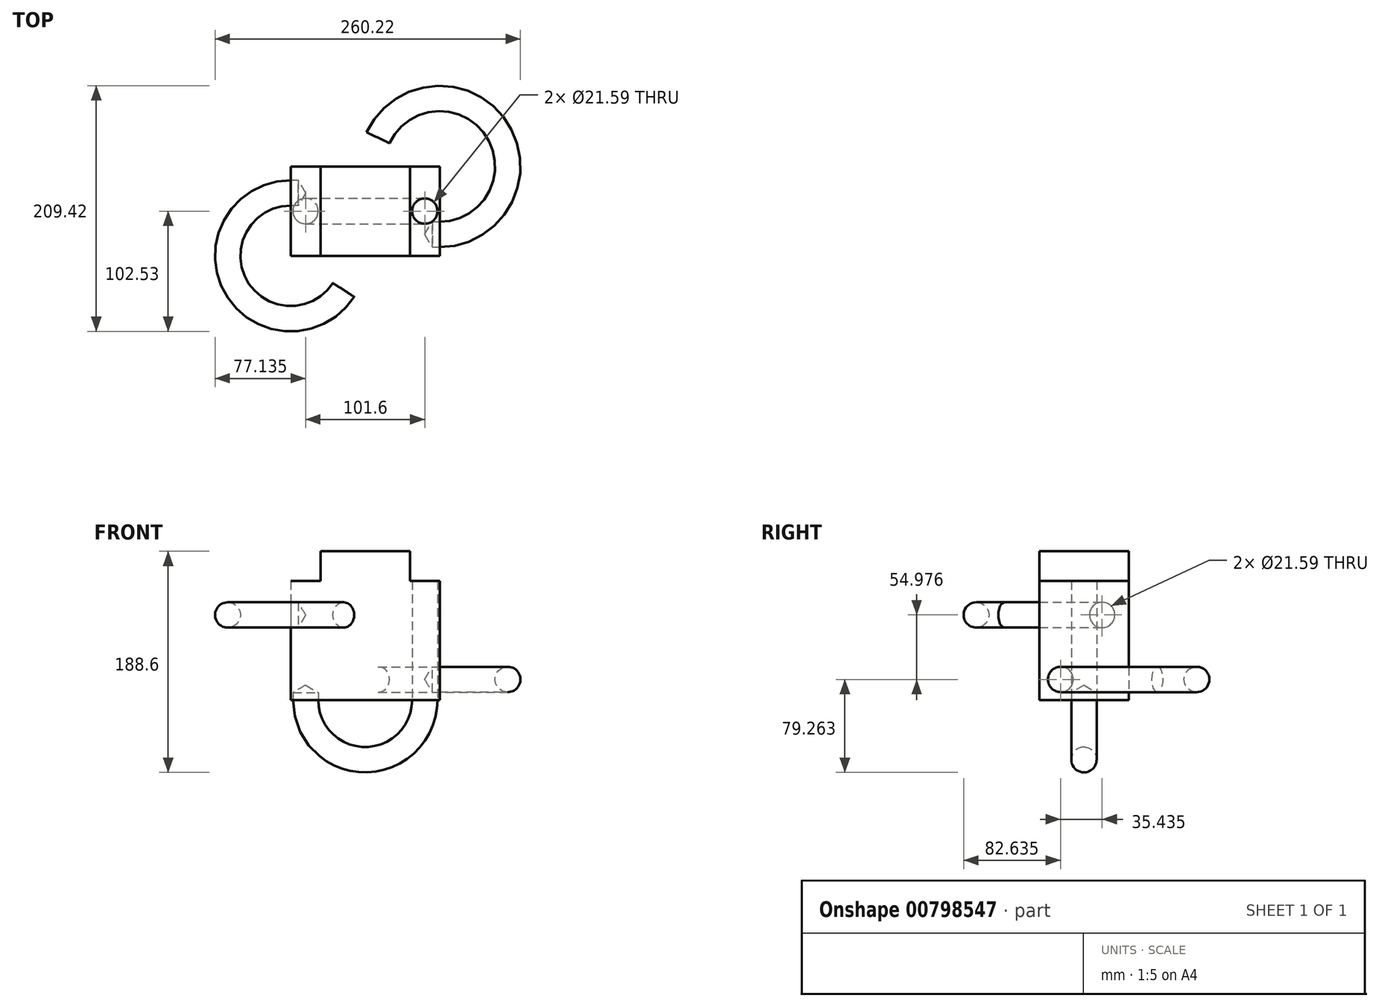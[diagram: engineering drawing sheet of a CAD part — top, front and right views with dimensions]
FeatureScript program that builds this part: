
annotation { "Feature Type Name" : "Feature", "Feature Type Description" : "" }
export const myFeature = defineFeature(function(context is Context, id is Id, definition is map)
    precondition{}
    {
        {
            var Q0;
            Q0=qCreatedBy(makeId("Top.planeOp"),FACE);
            var sketch = newSketch(context, id + "F0", { "sketchPlane" : qUnion([Q0])});
            skLineSegment(sketch, "E0.bottom", {"start": v(-20.13, 76.2) * mm, "end": v(106.87, 76.2) * mm});
            skLineSegment(sketch, "E0.top", {"start": v(-20.13, 0) * mm, "end": v(106.87, 0) * mm});
            skLineSegment(sketch, "E0.left", {"start": v(-20.13, 76.2) * mm, "end": v(-20.13, 0) * mm});
            skLineSegment(sketch, "E0.right", {"start": v(106.87, 76.2) * mm, "end": v(106.87, 0) * mm});
            skLineSegment(sketch, "E1.bottom", {"start": v(5.27, 76.2) * mm, "end": v(81.47, 76.2) * mm});
            skLineSegment(sketch, "E1.top", {"start": v(5.27, 0) * mm, "end": v(81.47, 0) * mm});
            skLineSegment(sketch, "E1.left", {"start": v(5.27, 76.2) * mm, "end": v(5.27, 0) * mm});
            skLineSegment(sketch, "E1.right", {"start": v(81.47, 76.2) * mm, "end": v(81.47, 0) * mm});
            skCircle(sketch, "E2", {"center": v(-7.43, 38.1) * mm, "radius": 10.8 * mm});
            skPoint(sketch, "E2.centerSnap0", {"position": v(-20.13, 38.1) * mm});
            skLineSegment(sketch, "E3", {"start": v(43.37, 0) * mm, "end": v(43.37, 76.2) * mm, "construction": true});
            skCircle(sketch, "E4.MirrorC", {"center": v(94.17, 38.1) * mm, "radius": 10.8 * mm});
            skSolve(sketch);
        }
        {
            var Q0;
            {var subQ0=sQuery(id+"F0.wireOp",EDGE,"E1.left");var subQ8=makeQuery(id+"F0.imprint","IMPRINT",EDGE,{"derivedFrom":subQ0});var subQ10=sQuery(id+"F0.wireOp",EDGE,"E0.left");var subQ11=sQuery(id+"F0.wireOp",EDGE,"E0.right");Q0=qUnion([makeQuery(id+"F0.imprint","IMPRINT",FACE,{"disambiguationData":[TD([[makeQuery(id+"F0.imprint","IMPRINT",EDGE,{"derivedFrom":subQ11}),-1.0]])]}),makeQuery(id+"F0.imprint","IMPRINT",FACE,{"disambiguationData":[TD([[makeQuery(id+"F0.imprint","IMPRINT",EDGE,{"derivedFrom":subQ10}),1.0]])]}),makeQuery(id+"F0.imprint","IMPRINT",FACE,{"disambiguationData":[TD([[subQ8,1.0]])]})]);}
            var Q1;
            Q1=makeQuery(id+"F0.imprint","IMPRINT",FACE,{"disambiguationData":[TD([[makeQuery(id+"F0.imprint","IMPRINT",EDGE,{"derivedFrom":sQuery(id+"F0.wireOp",EDGE,"E2")}),1.0]])]});
            var Q2;
            Q2=makeQuery(id+"F0.imprint","IMPRINT",FACE,{"disambiguationData":[TD([[makeQuery(id+"F0.imprint","IMPRINT",EDGE,{"derivedFrom":sQuery(id+"F0.wireOp",EDGE,"E4.MirrorC")}),-1.0]])]});
            extrude(context, id + "F1", {"entities" : qUnion([Q0, Q1, Q2]), "depth" : 101.6 * mm, "offsetDistance" : 25.4 * mm});
        }
        {
            var Q0;
            Q0=makeQuery(id+"F1.opExtrude","SWEPT_FACE",FACE,{"disambiguationData":[OSD([sQuery(id+"F0.wireOp",EDGE,"E0.left")])]});
            var sketch = newSketch(context, id + "F2", { "sketchPlane" : qUnion([Q0])});
            skCircle(sketch, "E5", {"center": v(-53.64, 72.64) * mm, "radius": 10.8 * mm});
            skSolve(sketch);
        }
        {
            var Q0;
            Q0=makeQuery(id+"F2.imprint","IMPRINT",FACE,{"disambiguationData":[TD([[makeQuery(id+"F2.imprint","IMPRINT",EDGE,{"derivedFrom":sQuery(id+"F2.wireOp",EDGE,"E5")}),1.0]])]});
            var Q1;
            Q1=makeQuery(id+"F1.opExtrude","SWEPT_EDGE",EDGE,{"disambiguationData":[OSD([sQuery(id+"F0.wireOp",EDGE,"E0.top"),sQuery(id+"F0.wireOp",EDGE,"E0.left")])]});
            revolve(context, id + "F3", {"surfaceOperationType" : NewSurfaceOperationType.NEW, "entities" : qUnion([Q0]), "axis" : qUnion([Q1]), "revolveType" : RevolveType.ONE_DIRECTION, "oppositeDirection" : true, "angle" : 237.17 * degree});
        }
        {
            var Q0;
            Q0=makeQuery(id+"F1.opExtrude","SWEPT_FACE",FACE,{"disambiguationData":[OSD([sQuery(id+"F0.wireOp",EDGE,"E0.right")])]});
            var sketch = newSketch(context, id + "F4", { "sketchPlane" : qUnion([Q0])});
            skCircle(sketch, "E6", {"center": v(18.2, 17.66) * mm, "radius": 10.8 * mm});
            skSolve(sketch);
        }
        {
            var Q0;
            Q0=makeQuery(id+"F4.imprint","IMPRINT",FACE,{"disambiguationData":[TD([[makeQuery(id+"F4.imprint","IMPRINT",EDGE,{"derivedFrom":sQuery(id+"F4.wireOp",EDGE,"E6")}),1.0]])]});
            var Q1;
            Q1=makeQuery(id+"F1.opExtrude","SWEPT_EDGE",EDGE,{"disambiguationData":[OSD([sQuery(id+"F0.wireOp",EDGE,"E0.bottom"),sQuery(id+"F0.wireOp",EDGE,"E0.right")])]});
            revolve(context, id + "F5", {"surfaceOperationType" : NewSurfaceOperationType.NEW, "entities" : qUnion([Q0]), "axis" : qUnion([Q1]), "revolveType" : RevolveType.ONE_DIRECTION, "oppositeDirection" : true, "angle" : 245 * degree});
        }
        {
            var Q0;
            {var subQ0=sQuery(id+"F0.wireOp",EDGE,"E1.left");Q0=makeQuery(id+"F0.imprint","IMPRINT",FACE,{"disambiguationData":[TD([[makeQuery(id+"F0.imprint","IMPRINT",EDGE,{"derivedFrom":subQ0}),1.0]])]});}
            extrude(context, id + "F6", {"entities" : qUnion([Q0]), "operationType" : NewBodyOperationType.ADD, "depth" : 127 * mm, "offsetDistance" : 25.4 * mm});
        }
        {
            var Q0;
            Q0=makeQuery(id+"F0.imprint","IMPRINT",FACE,{"disambiguationData":[TD([[makeQuery(id+"F0.imprint","IMPRINT",EDGE,{"derivedFrom":sQuery(id+"F0.wireOp",EDGE,"E2")}),1.0]])]});
            var Q1;
            Q1=sQuery(id+"F0.wireOp",EDGE,"E3");
            revolve(context, id + "F7", {"surfaceOperationType" : NewSurfaceOperationType.NEW, "entities" : qUnion([Q0]), "axis" : qUnion([Q1]), "revolveType" : RevolveType.ONE_DIRECTION, "oppositeDirection" : true, "angle" : 180 * degree});
        }
        {
            var Q0;
            Q0=sQuery(id+"F4.wireOp",VERTEX,"E6.center");
            var Q1;
            Q1=makeQuery(id+"F1.opExtrude","SWEPT_BODY",BODY,{"disambiguationData":[OSD([sQuery(id+"F0.wireOp",EDGE,"E0.bottom"),sQuery(id+"F0.wireOp",EDGE,"E0.top"),sQuery(id+"F0.wireOp",EDGE,"E0.left"),sQuery(id+"F0.wireOp",EDGE,"E0.right")])]});
            hole(context, id + "F8", {"style" : HoleStyle.SIMPLE, "endStyle" : HoleEndStyle.BLIND, "holeDiameter" : 21.59 * mm, "majorDiameter" : 6.35 * mm, "holeDepth" : 6.35 * mm, "isTappedThrough" : true, "tappedDepth" : 0.33 * mm, "tapClearance" : 3, "startFromSketch" : true, "locations" : qUnion([Q0]), "scope" : qUnion([Q1])});
        }
        {
            var Q0;
            Q0=sQuery(id+"F2.wireOp",VERTEX,"E5.center");
            var Q1;
            Q1=makeQuery(id+"F1.opExtrude","SWEPT_BODY",BODY,{"disambiguationData":[OSD([sQuery(id+"F0.wireOp",EDGE,"E0.bottom"),sQuery(id+"F0.wireOp",EDGE,"E0.top"),sQuery(id+"F0.wireOp",EDGE,"E0.left"),sQuery(id+"F0.wireOp",EDGE,"E0.right")])]});
            hole(context, id + "F9", {"style" : HoleStyle.SIMPLE, "endStyle" : HoleEndStyle.BLIND, "holeDiameter" : 21.59 * mm, "majorDiameter" : 6.35 * mm, "holeDepth" : 6.35 * mm, "isTappedThrough" : true, "tappedDepth" : 0.33 * mm, "tapClearance" : 3, "startFromSketch" : true, "locations" : qUnion([Q0]), "scope" : qUnion([Q1])});
        }
        {
            var Q0;
            Q0=sQuery(id+"F0.wireOp",VERTEX,"E2.center");
            var Q1;
            Q1=makeQuery(id+"F1.opExtrude","SWEPT_BODY",BODY,{"disambiguationData":[OSD([sQuery(id+"F0.wireOp",EDGE,"E0.bottom"),sQuery(id+"F0.wireOp",EDGE,"E0.top"),sQuery(id+"F0.wireOp",EDGE,"E0.left"),sQuery(id+"F0.wireOp",EDGE,"E0.right")])]});
            hole(context, id + "F10", {"style" : HoleStyle.SIMPLE, "endStyle" : HoleEndStyle.BLIND, "oppositeDirection" : true, "holeDiameter" : 21.59 * mm, "majorDiameter" : 6.35 * mm, "holeDepth" : 6.35 * mm, "isTappedThrough" : true, "tappedDepth" : 0.33 * mm, "tapClearance" : 3, "startFromSketch" : true, "locations" : qUnion([Q0]), "scope" : qUnion([Q1])});
        }
        {
            var Q0;
            Q0=sQuery(id+"F0.wireOp",VERTEX,"E4.MirrorC.center");
            var Q1;
            Q1=makeQuery(id+"F1.opExtrude","SWEPT_BODY",BODY,{"disambiguationData":[OSD([sQuery(id+"F0.wireOp",EDGE,"E0.bottom"),sQuery(id+"F0.wireOp",EDGE,"E0.top"),sQuery(id+"F0.wireOp",EDGE,"E0.left"),sQuery(id+"F0.wireOp",EDGE,"E0.right")])]});
            hole(context, id + "F11", {"style" : HoleStyle.SIMPLE, "endStyle" : HoleEndStyle.BLIND, "oppositeDirection" : true, "holeDiameter" : 21.59 * mm, "majorDiameter" : 6.35 * mm, "holeDepth" : 6.35 * mm, "isTappedThrough" : true, "tappedDepth" : 0.33 * mm, "tapClearance" : 3, "startFromSketch" : true, "locations" : qUnion([Q0]), "scope" : qUnion([Q1])});
        }
    });
